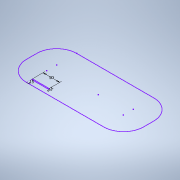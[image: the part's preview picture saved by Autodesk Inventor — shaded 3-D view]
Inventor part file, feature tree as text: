
AUTODESK INVENTOR PART (.ipt)
format: ipt  version: 2022 (Build 260153000, 153)  size: 92,672 bytes
history: native  units: mm
features: sketch x1
ambient origin geometry x8: Origin, YZ Plane, XZ Plane, XY Plane, X Axis, Y Axis, Z Axis, Center Point
feature tree (1):
  sketch  "Boceto1"  dims[d2=50.0mm d3=3.0mm d4=15.0mm]
